# Revit family: Safety-Railing_Section_SafetyRail_Mobile-SelfClosingGateFrame
name_source: partatom
category: Railings
units: mm (PartAtom-declared; Revit-internal decimal feet)

## family parameters
Classification Number = 23.30.80.11
Cut with Voids When Loaded = No
Shared = No

## types (1)
- as Specified
    Base Weight = 104 lbs per Base Plate
    Clear Opening Width = 2' - 7 1/4"
    Construction Details = http://www.arcat.com
    Description = Safety Rail Company Non-Penetrating Fall Protection System - 360 Mobile Self-Closing Frame and Gate as Specified
    Expected Lifespan (Years) = 0
    Green Building-LEED = http://www.arcat.com
    Height Adjustment Required = 0' - 0"
    Keynote = 05 52 00
    Maintenance Schedule (Months) = 0
    Manufacturer = Safety Rail Company
    Manufacturer Fax = 888-471-4931
    Manufacturer Website = http://www.safetyrailcompany.com
    Model = SRC 360 Mobile Self-Closing Frame and Gate
    Post OD = 0' - 1 5/8"
    Product Data = http://www.arcat.com
    Product Properties = http://www.safetyrailcompany.com
    Revision = R1_2017-08
    Sales Information = http://www.safetyrailcompany.com
    SpecWizard = http://www.arcat.com
    Specification = http://www.arcat.com
    Standards Conformance = OSHA Guardrail Reg 1910.23, 1926.500 - .503  ;  Made in USA
    URL = http://www.safetyrailcompany.com
    Unit Height = 3' - 7 11/16"
    Unit Length = 0' - 5"
    Warranty Duration (Years) = 0

## geometry (parser evidence)
native form markers: Sweep x9
no freeform markers — native parametric forms only
